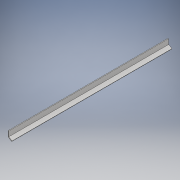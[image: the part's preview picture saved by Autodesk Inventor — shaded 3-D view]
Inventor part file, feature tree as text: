
AUTODESK INVENTOR PART (.ipt)
format: ipt  version: 2018 (Build 220112000, 112)  size: 100,352 bytes
history: native  units: mm
features: other x1, extrude x1, sketch x1
ambient origin geometry x8: Origin, YZ Plane, XZ Plane, XY Plane, X Axis, Y Axis, Z Axis, Center Point
bodies: Body1 (feature_tree)
feature tree (3):
  other  "ソリッド1"
  extrude  "押し出し1"  Depth=7.0mm
  sketch  "スケッチ1"
